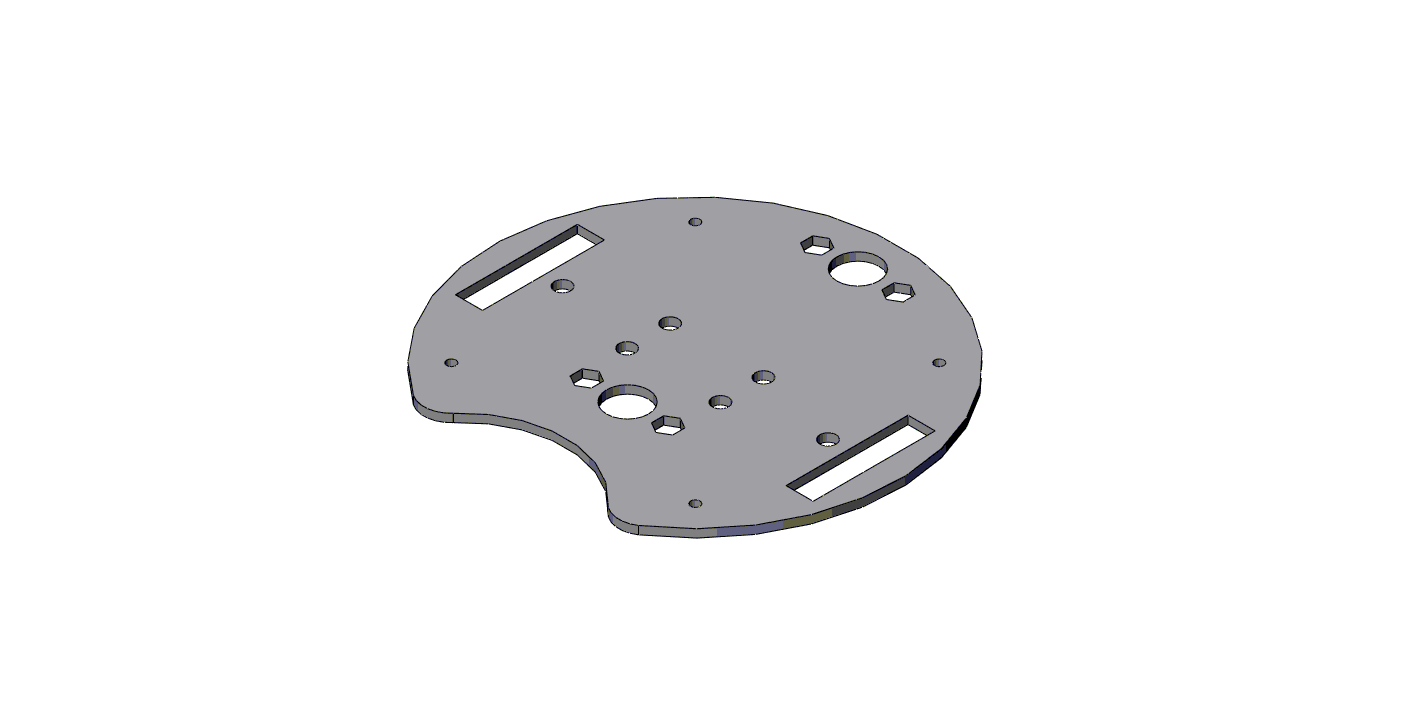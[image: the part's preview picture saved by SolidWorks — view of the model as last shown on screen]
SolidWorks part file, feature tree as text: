
SOLIDWORKS PART (.sldprt)
format: sldprt  version: not decoded by parser v0  size: 373,760 bytes
history: native  units: mm
features: sketch x7, cut_extrude x6, material x1, extrude x1, fillet x1 (+13 scaffold rows collapsed)
feature tree (29):
  scaffold x13  (default folders/planes/origin — collapsed)
  material  "Material <not specified>"
  sketch  "Sketch1"  dims[D1=150.0mm]
  extrude  "Boss-Extrude1"  Depth=3mm
  sketch  "Sketch2"  dims[D1=45.0mm D2=45.0mm D3=10.0mm D4=10.0mm D5=61.0mm D6=61.0mm]
  cut_extrude  "Cut-Extrude1"  Depth=6.35mm
  sketch  "Sketch3"  dims[c1.D1=15.5mm c1.D3=7.0mm c1.D4=7.0mm c2.D1=15.5mm c2.D2=15.5mm c2.D3=15.5mm c3.D2=14.732mm c3.D5=14.732mm c3.D6=60.0mm c3.D7=25.0mm]
  cut_extrude  "Cut-Extrude2"  Depth=10mm
  sketch  "Sketch4"  dims[c1.D1=76.2mm c1.D2=~27.195139mm c2.D2=121.0deg]
  cut_extrude  "Cut-Extrude3"  Depth=10mm
  fillet  "Fillet2"  Radius=10mm
  sketch  "Sketch6"  dims[c1.D1=3.429mm c1.D3=3.429mm c1.D2=30.0mm c1.D4=30.0mm c2.D1=7.7978mm c2.D5=7.7978mm c2.D3=7.7978mm c2.D6=7.7978mm]
  sketch  "Sketch7"  dims[c1.D1=4.3053mm c2.D1=6.0mm c2.D2=9.525mm c2.D3=31.75mm c2.D4=15.875mm c2.D5=2.5mm c3.D1=7.7978mm c3.D6=7.7978mm c3.D7=7.7978mm]
  cut_extrude  "Cut-Extrude5"  Depth=3mm
  cut_extrude  "Cut-Extrude6"  Depth=3mm
  sketch  "Sketch8"  dims[D3=3.429mm D1=90.0mm D2=90.0mm]
  cut_extrude  "Cut-Extrude7"  Depth=10mm
decode coverage: 15 of 15 modeling features carry decoded parameters
note: ~ marks probable driven/reference dimensions
note: suppression state not decoded; provenance and decode notes live in map.json
